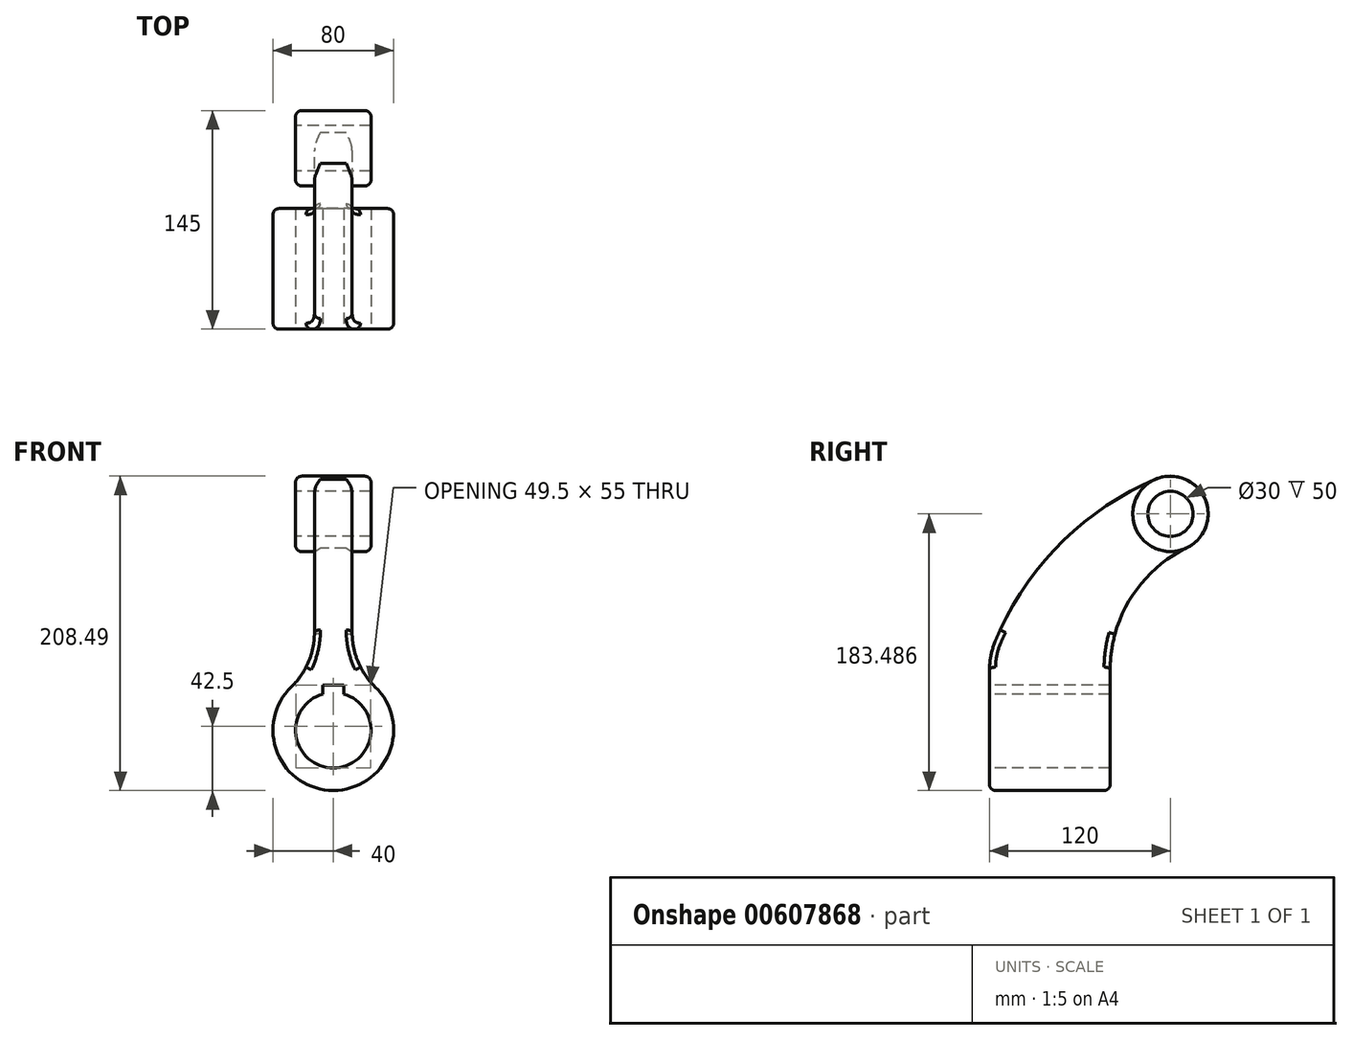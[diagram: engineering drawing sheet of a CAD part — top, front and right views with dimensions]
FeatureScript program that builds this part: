
annotation { "Feature Type Name" : "Feature", "Feature Type Description" : "" }
export const myFeature = defineFeature(function(context is Context, id is Id, definition is map)
    precondition{}
    {
        {
            var Q0;
            Q0=qCreatedBy(makeId("Right.planeOp"),FACE);
            var sketch = newSketch(context, id + "F0", { "sketchPlane" : qUnion([Q0])});
            skLineSegment(sketch, "E0.bottom", {"start": v(0, 0) * mm, "end": v(80, 0) * mm});
            skLineSegment(sketch, "E0.top", {"start": v(0, 15) * mm, "end": v(80, 15) * mm});
            skLineSegment(sketch, "E0.left", {"start": v(0, 0) * mm, "end": v(0, 15) * mm});
            skLineSegment(sketch, "E0.right", {"start": v(80, 0) * mm, "end": v(80, 15) * mm});
            skCircle(sketch, "E1", {"center": v(120, 118.49) * mm, "radius": 25 * mm});
            skCircle(sketch, "E2", {"center": v(120, 118.49) * mm, "radius": 15 * mm});
            skArc(sketch, "E3", {"start": v(130.2, 95.66) * mm, "mid": v(93.58, 62.5) * mm, "end": v(80, 15) * mm});
            skArc(sketch, "E4", {"start": v(3.83, 34.18) * mm, "mid": v(0.97, 24.78) * mm, "end": v(0, 15) * mm});
            skArc(sketch, "E5", {"start": v(109.9, 141.35) * mm, "mid": v(46.37, 98.15) * mm, "end": v(3.83, 34.18) * mm});
            skLineSegment(sketch, "E6", {"start": v(0, -25) * mm, "end": v(80, -25) * mm, "construction": true});
            skSolve(sketch);
        }
        {
            var Q0;
            Q0=makeQuery(id+"F0.imprint","IMPRINT",FACE,{"disambiguationData":[TD([[makeQuery(id+"F0.imprint","IMPRINT",EDGE,{"derivedFrom":sQuery(id+"F0.wireOp",EDGE,"E0.bottom")}),1.0]])]});
            var Q1;
            Q1=sQuery(id+"F0.wireOp",EDGE,"E6");
            revolve(context, id + "F1", {"entities" : qUnion([Q0]), "axis" : qUnion([Q1]), "revolveType" : RevolveType.FULL});
        }
        {
            var Q0;
            Q0=makeQuery(id+"F0.imprint","IMPRINT",FACE,{"disambiguationData":[TD([[makeQuery(id+"F0.imprint","IMPRINT",EDGE,{"derivedFrom":sQuery(id+"F0.wireOp",EDGE,"E0.top")}),1.0]])]});
            var Q1;
            Q1=makeQuery(id+"F0.imprint","IMPRINT",FACE,{"disambiguationData":[TD([[makeQuery(id+"F0.imprint","IMPRINT",EDGE,{"derivedFrom":sQuery(id+"F0.wireOp",EDGE,"E0.bottom")}),1.0]])]});
            extrude(context, id + "F2", {"entities" : qUnion([Q0, Q1]), "operationType" : NewBodyOperationType.ADD, "endBound" : BoundingType.SYMMETRIC, "depth" : 25 * mm, "offsetDistance" : 25 * mm});
        }
        {
            var Q0;
            Q0=makeQuery(id+"F0.imprint","IMPRINT",FACE,{"disambiguationData":[TD([[makeQuery(id+"F0.imprint","IMPRINT",EDGE,{"derivedFrom":sQuery(id+"F0.wireOp",EDGE,"E2")}),-1.0]])]});
            extrude(context, id + "F3", {"entities" : qUnion([Q0]), "operationType" : NewBodyOperationType.ADD, "endBound" : BoundingType.SYMMETRIC, "depth" : 50 * mm, "offsetDistance" : 25 * mm});
        }
        {
            var Q0;
            Q0=makeQuery(id+"F2.boolean.opBoolean","INTERSECT",EDGE,{"derivedFrom":[makeQuery(id+"F1.opRevolve","SWEPT_FACE",FACE,{"disambiguationData":[OSD([sQuery(id+"F0.wireOp",EDGE,"E0.top")])]}),makeQuery(id+"F2.opExtrude","CAP_FACE",FACE,{"disambiguationData":[OSD([sQuery(id+"F0.wireOp",EDGE,"E0.bottom"),sQuery(id+"F0.wireOp",EDGE,"E0.left"),sQuery(id+"F0.wireOp",EDGE,"E0.right"),sQuery(id+"F0.wireOp",EDGE,"E1"),sQuery(id+"F0.wireOp",EDGE,"E3"),sQuery(id+"F0.wireOp",EDGE,"E4"),sQuery(id+"F0.wireOp",EDGE,"E5")])],"isStart":false})]});
            fillet(context, id + "F4", {"entities" : qUnion([Q0]), "radius" : 50 * mm, "tangentPropagation" : true, "allowEdgeOverflow" : false});
        }
        {
            var Q0;
            Q0=makeQuery(id+"F2.boolean.opBoolean","INTERSECT",EDGE,{"derivedFrom":[makeQuery(id+"F1.opRevolve","SWEPT_FACE",FACE,{"disambiguationData":[OSD([sQuery(id+"F0.wireOp",EDGE,"E0.top")])]}),makeQuery(id+"F2.opExtrude","CAP_FACE",FACE,{"disambiguationData":[OSD([sQuery(id+"F0.wireOp",EDGE,"E0.bottom"),sQuery(id+"F0.wireOp",EDGE,"E0.left"),sQuery(id+"F0.wireOp",EDGE,"E0.right"),sQuery(id+"F0.wireOp",EDGE,"E1"),sQuery(id+"F0.wireOp",EDGE,"E3"),sQuery(id+"F0.wireOp",EDGE,"E4"),sQuery(id+"F0.wireOp",EDGE,"E5")])],"isStart":true})]});
            fillet(context, id + "F5", {"entities" : qUnion([Q0]), "radius" : 50 * mm, "tangentPropagation" : true, "allowEdgeOverflow" : false});
        }
        {
            var Q0;
            Q0=makeQuery(id+"F3.opExtrude","CAP_EDGE",EDGE,{"disambiguationData":[OSD([sQuery(id+"F0.wireOp",EDGE,"E1")])],"isStart":true});
            fillet(context, id + "F6", {"entities" : qUnion([Q0]), "radius" : 4 * mm, "tangentPropagation" : true, "allowEdgeOverflow" : false});
        }
        {
            var Q0;
            Q0=makeQuery(id+"F2.opExtrude","CAP_EDGE",EDGE,{"disambiguationData":[OSD([sQuery(id+"F0.wireOp",EDGE,"E5")])],"isStart":true});
            fillet(context, id + "F7", {"entities" : qUnion([Q0]), "radius" : 4 * mm, "tangentPropagation" : true, "allowEdgeOverflow" : false});
        }
        {
            var Q0;
            Q0=makeQuery(id+"F1.opRevolve","SWEPT_EDGE",EDGE,{"disambiguationData":[OSD([sQuery(id+"F0.wireOp",EDGE,"E0.top"),sQuery(id+"F0.wireOp",EDGE,"E0.right"),sQuery(id+"F0.wireOp",EDGE,"E3")])]});
            fillet(context, id + "F8", {"entities" : qUnion([Q0]), "radius" : 4 * mm, "tangentPropagation" : true, "allowEdgeOverflow" : false});
        }
        {
            var Q0;
            Q0=makeQuery(id+"F3.opExtrude","CAP_EDGE",EDGE,{"disambiguationData":[OSD([sQuery(id+"F0.wireOp",EDGE,"E1")])],"isStart":false});
            fillet(context, id + "F9", {"entities" : qUnion([Q0]), "radius" : 4 * mm, "tangentPropagation" : true, "allowEdgeOverflow" : false});
        }
        {
            var Q0;
            Q0=qCreatedBy(makeId("Front.planeOp"),FACE);
            var sketch = newSketch(context, id + "F10", { "sketchPlane" : qUnion([Q0])});
            skLineSegment(sketch, "E7.bottom", {"start": v(-7, 5) * mm, "end": v(7, 5) * mm});
            skLineSegment(sketch, "E8", {"start": v(-7, 5) * mm, "end": v(-7, -25) * mm});
            skLineSegment(sketch, "E9", {"start": v(-7, -25) * mm, "end": v(7, -25) * mm});
            skLineSegment(sketch, "E10", {"start": v(7, 5) * mm, "end": v(7, -25) * mm});
            skSolve(sketch);
        }
        {
            var Q0;
            Q0 = qSketchRegion(id + "F10", true);
            extrude(context, id + "F11", {"entities" : qUnion([Q0]), "operationType" : NewBodyOperationType.REMOVE, "endBound" : BoundingType.THROUGH_ALL, "oppositeDirection" : true, "depth" : 25 * mm, "offsetDistance" : 25 * mm});
        }
    });
